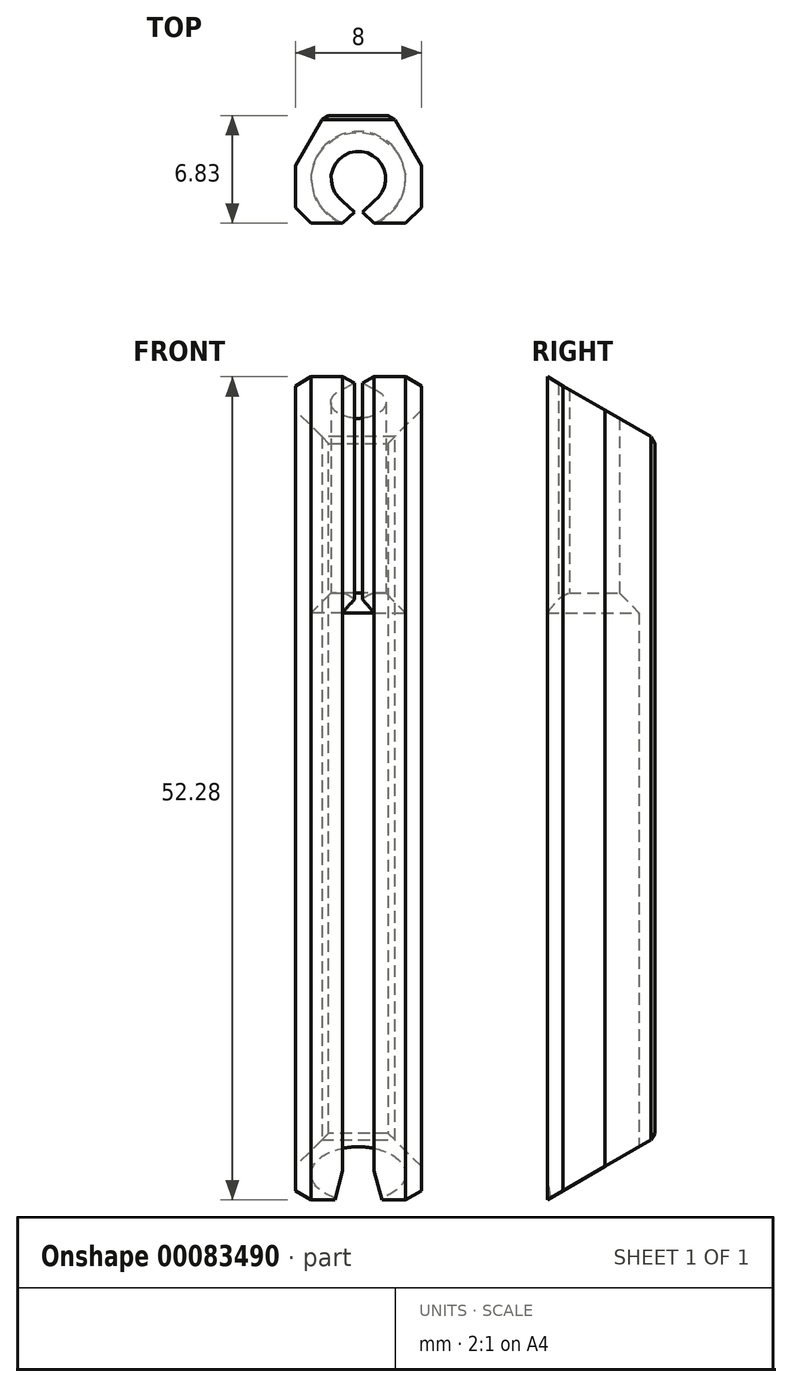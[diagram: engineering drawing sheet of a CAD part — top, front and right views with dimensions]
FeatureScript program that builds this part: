
annotation { "Feature Type Name" : "Feature", "Feature Type Description" : "" }
export const myFeature = defineFeature(function(context is Context, id is Id, definition is map)
    precondition{}
    {
        {
            var Q0;
            Q0=qCreatedBy(makeId("Top.planeOp"),FACE);
            var sketch = newSketch(context, id + "F0", { "sketchPlane" : qUnion([Q0])});
            skArc(sketch, "E0", {"start": v(1, -2.83) * mm, "mid": v(0, 3) * mm, "end": v(-1, -2.83) * mm});
            skLineSegment(sketch, "E1", {"start": v(-1, -3) * mm, "end": v(1, -3) * mm, "construction": true});
            skPoint(sketch, "E2", {"position": v(0, -3) * mm});
            skLineSegment(sketch, "E3", {"start": v(0, -3) * mm, "end": v(0, 4) * mm, "construction": true});
            skLineSegment(sketch, "E4", {"start": v(-1, -3) * mm, "end": v(-1, -2.83) * mm});
            skLineSegment(sketch, "E5", {"start": v(-1, -3) * mm, "end": v(-4, -3) * mm});
            skLineSegment(sketch, "E6", {"start": v(-4, -3) * mm, "end": v(-4, 4) * mm});
            skLineSegment(sketch, "E7", {"start": v(-4, 4) * mm, "end": v(0, 4) * mm});
            skLineSegment(sketch, "E8.MirrorCS", {"start": v(4, 4) * mm, "end": v(0, 4) * mm});
            skLineSegment(sketch, "E9.MirrorCS", {"start": v(4, -3) * mm, "end": v(4, 4) * mm});
            skLineSegment(sketch, "E10.MirrorCS", {"start": v(1, -3) * mm, "end": v(4, -3) * mm});
            skLineSegment(sketch, "E11.MirrorCS", {"start": v(1, -3) * mm, "end": v(1, -2.83) * mm});
            skPoint(sketch, "E12", {"position": v(0, 3) * mm});
            skSolve(sketch);
        }
        {
            var Q0;
            Q0 = qSketchRegion(id + "F0", true);
            extrude(context, id + "F1", {"entities" : qUnion([Q0]), "depth" : 20 * mm});
        }
        {
            var Q0;
            Q0=makeQuery(id+"F1.opExtrude","CAP_FACE",FACE,{"disambiguationData":[OSD([sQuery(id+"F0.wireOp",EDGE,"E0"),sQuery(id+"F0.wireOp",EDGE,"E4"),sQuery(id+"F0.wireOp",EDGE,"E5"),sQuery(id+"F0.wireOp",EDGE,"E6"),sQuery(id+"F0.wireOp",EDGE,"E7"),sQuery(id+"F0.wireOp",EDGE,"E8.MirrorCS"),sQuery(id+"F0.wireOp",EDGE,"E9.MirrorCS"),sQuery(id+"F0.wireOp",EDGE,"E10.MirrorCS"),sQuery(id+"F0.wireOp",EDGE,"E11.MirrorCS")])],"isStart":false});
            extrude(context, id + "F2", {"entities" : qUnion([Q0]), "operationType" : NewBodyOperationType.ADD, "depth" : 15 * mm});
        }
        {
            var Q0;
            Q0=makeQuery(id+"F2.opExtrude","CAP_FACE",FACE,{"disambiguationData":[OSD([sQuery(id+"F0.wireOp",EDGE,"E0"),sQuery(id+"F0.wireOp",EDGE,"E4"),sQuery(id+"F0.wireOp",EDGE,"E5"),sQuery(id+"F0.wireOp",EDGE,"E6"),sQuery(id+"F0.wireOp",EDGE,"E7"),sQuery(id+"F0.wireOp",EDGE,"E8.MirrorCS"),sQuery(id+"F0.wireOp",EDGE,"E9.MirrorCS"),sQuery(id+"F0.wireOp",EDGE,"E10.MirrorCS"),sQuery(id+"F0.wireOp",EDGE,"E11.MirrorCS")])],"isStart":false});
            var sketch = newSketch(context, id + "F3", { "sketchPlane" : qUnion([Q0])});
            skLineSegment(sketch, "E13.bottom", {"start": v(-4, -2.83) * mm, "end": v(4, -2.83) * mm});
            skLineSegment(sketch, "E13.top", {"start": v(-4, -3) * mm, "end": v(4, -3) * mm});
            skLineSegment(sketch, "E13.left", {"start": v(-4, -2.83) * mm, "end": v(-4, -3) * mm});
            skLineSegment(sketch, "E13.right", {"start": v(4, -2.83) * mm, "end": v(4, -3) * mm});
            skSolve(sketch);
        }
        {
            var Q0;
            Q0 = qSketchRegion(id + "F3", true);
            extrude(context, id + "F4", {"entities" : qUnion([Q0]), "operationType" : NewBodyOperationType.REMOVE, "endBound" : BoundingType.THROUGH_ALL, "oppositeDirection" : true, "depth" : 25 * mm});
        }
        {
            var Q0;
            Q0=makeQuery(id+"F2.opExtrude","CAP_FACE",FACE,{"disambiguationData":[OSD([sQuery(id+"F0.wireOp",EDGE,"E0"),sQuery(id+"F0.wireOp",EDGE,"E4"),sQuery(id+"F0.wireOp",EDGE,"E5"),sQuery(id+"F0.wireOp",EDGE,"E6"),sQuery(id+"F0.wireOp",EDGE,"E7"),sQuery(id+"F0.wireOp",EDGE,"E8.MirrorCS"),sQuery(id+"F0.wireOp",EDGE,"E9.MirrorCS"),sQuery(id+"F0.wireOp",EDGE,"E10.MirrorCS"),sQuery(id+"F0.wireOp",EDGE,"E11.MirrorCS")])],"isStart":false});
            var sketch = newSketch(context, id + "F5", { "sketchPlane" : qUnion([Q0])});
            skArc(sketch, "E14", {"start": v(1, -1.44) * mm, "mid": v(0, 1.75) * mm, "end": v(-1, -1.44) * mm});
            skLineSegment(sketch, "E15", {"start": v(-1, -1.44) * mm, "end": v(-0.25, -2.13) * mm});
            skLineSegment(sketch, "E16", {"start": v(-0.25, -2.13) * mm, "end": v(-1, -2.83) * mm});
            skLineSegment(sketch, "E17", {"start": v(0, -1.75) * mm, "end": v(0, -2.83) * mm, "construction": true});
            skLineSegment(sketch, "E18.MirrorCS", {"start": v(1, -1.44) * mm, "end": v(0.25, -2.13) * mm});
            skLineSegment(sketch, "E19.MirrorCS", {"start": v(0.25, -2.13) * mm, "end": v(1, -2.83) * mm});
            skLineSegment(sketch, "E20.0", {"start": v(1, -2.83) * mm, "end": v(4, -2.83) * mm});
            skLineSegment(sketch, "E20.1", {"start": v(4, -2.83) * mm, "end": v(4, 4) * mm});
            skLineSegment(sketch, "E20.2", {"start": v(4, 4) * mm, "end": v(-4, 4) * mm});
            skLineSegment(sketch, "E20.3", {"start": v(-4, -2.83) * mm, "end": v(-4, 4) * mm});
            skLineSegment(sketch, "E20.4", {"start": v(-4, -2.83) * mm, "end": v(-1, -2.83) * mm});
            skSolve(sketch);
        }
        {
            var Q0;
            Q0 = qSketchRegion(id + "F5", true);
            extrude(context, id + "F6", {"entities" : qUnion([Q0]), "operationType" : NewBodyOperationType.ADD, "depth" : 15 * mm});
        }
        {
            var Q0;
            Q0=makeQuery(id+"F6.opExtrude","CAP_EDGE",EDGE,{"disambiguationData":[OSD([sQuery(id+"F5.wireOp",EDGE,"E14")])],"isStart":true});
            chamfer(context, id + "F7", {"entities" : qUnion([Q0]), "width" : ((6 - 3.5) / 2) * mm, "tangentPropagation" : true});
        }
        {
            var Q0;
            Q0=makeQuery(id+"F1.opExtrude","CAP_FACE",FACE,{"disambiguationData":[OSD([sQuery(id+"F0.wireOp",EDGE,"E0"),sQuery(id+"F0.wireOp",EDGE,"E4"),sQuery(id+"F0.wireOp",EDGE,"E5"),sQuery(id+"F0.wireOp",EDGE,"E6"),sQuery(id+"F0.wireOp",EDGE,"E7"),sQuery(id+"F0.wireOp",EDGE,"E8.MirrorCS"),sQuery(id+"F0.wireOp",EDGE,"E9.MirrorCS"),sQuery(id+"F0.wireOp",EDGE,"E10.MirrorCS"),sQuery(id+"F0.wireOp",EDGE,"E11.MirrorCS")])],"isStart":true});
            extrude(context, id + "F8", {"entities" : qUnion([Q0]), "operationType" : NewBodyOperationType.ADD, "depth" : 7.9 * mm});
        }
        {
            var Q0;
            Q0=makeQuery(id+"F8.opExtrude","CAP_FACE",FACE,{"disambiguationData":[OSD([sQuery(id+"F0.wireOp",EDGE,"E0"),sQuery(id+"F0.wireOp",EDGE,"E4"),sQuery(id+"F0.wireOp",EDGE,"E5"),sQuery(id+"F0.wireOp",EDGE,"E6"),sQuery(id+"F0.wireOp",EDGE,"E7"),sQuery(id+"F0.wireOp",EDGE,"E8.MirrorCS"),sQuery(id+"F0.wireOp",EDGE,"E9.MirrorCS"),sQuery(id+"F0.wireOp",EDGE,"E10.MirrorCS"),sQuery(id+"F0.wireOp",EDGE,"E11.MirrorCS")])],"isStart":false});
            var sketch = newSketch(context, id + "F9", { "sketchPlane" : qUnion([Q0])});
            skLineSegment(sketch, "E21.bottom", {"start": v(-4, -4) * mm, "end": v(4, -4) * mm});
            skLineSegment(sketch, "E21.top", {"start": v(-4, 2.83) * mm, "end": v(4, 2.83) * mm});
            skLineSegment(sketch, "E21.left", {"start": v(-4, -4) * mm, "end": v(-4, 2.83) * mm});
            skLineSegment(sketch, "E21.right", {"start": v(4, -4) * mm, "end": v(4, 2.83) * mm});
            skSolve(sketch);
        }
        {
            var Q0;
            Q0 = qSketchRegion(id + "F9", true);
            extrude(context, id + "F10", {"entities" : qUnion([Q0]), "operationType" : NewBodyOperationType.ADD, "depth" : 3 * mm});
        }
        {
            var Q0;
            {var subQ0=sQuery(id+"F0.wireOp",EDGE,"E6");Q0=makeQuery(id+"F10.boolean.opBoolean","MERGE",FACE,{"derivedFrom":[makeQuery(id+"F8.boolean.opBoolean","MERGE",FACE,{"derivedFrom":[makeQuery(id+"F6.boolean.opBoolean","MERGE",FACE,{"derivedFrom":[makeQuery(id+"F2.boolean.opBoolean","MERGE",FACE,{"derivedFrom":[makeQuery(id+"F1.opExtrude","SWEPT_FACE",FACE,{"disambiguationData":[OSD([subQ0])]}),makeQuery(id+"F2.opExtrude","SWEPT_FACE",FACE,{"disambiguationData":[OSD([subQ0])]})]}),makeQuery(id+"F6.opExtrude","SWEPT_FACE",FACE,{"disambiguationData":[OSD([sQuery(id+"F5.wireOp",EDGE,"E20.3")])]})]}),makeQuery(id+"F8.opExtrude","SWEPT_FACE",FACE,{"disambiguationData":[OSD([subQ0])]})]}),makeQuery(id+"F10.opExtrude","SWEPT_FACE",FACE,{"disambiguationData":[OSD([sQuery(id+"F9.wireOp",EDGE,"E21.left")])]})]});}
            var sketch = newSketch(context, id + "F11", { "sketchPlane" : qUnion([Q0])});
            skLineSegment(sketch, "E22", {"start": v(-5, -12.23) * mm, "end": v(-5, 5.13) * mm});
            skLineSegment(sketch, "E23", {"start": v(-5, 5.13) * mm, "end": v(-2.5, 0.8) * mm});
            skLineSegment(sketch, "E24", {"start": v(-2.5, 0.8) * mm, "end": v(-2.5, -7.9) * mm});
            skLineSegment(sketch, "E25", {"start": v(-2.5, -7.9) * mm, "end": v(-5, -12.23) * mm});
            skLineSegment(sketch, "E26.0", {"start": v(-3, -7.9) * mm, "end": v(2.83, -7.9) * mm, "construction": true});
            skLineSegment(sketch, "E27.0", {"start": v(0, -15.9) * mm, "end": v(-5, -15.9) * mm, "construction": true});
            skSolve(sketch);
        }
        {
            var Q0;
            {var subQ0=sQuery(id+"F3.wireOp",EDGE,"E13.bottom");var subQ1=makeQuery(id+"F4.opExtrude","SWEPT_FACE",FACE,{"disambiguationData":[OSD([subQ0])]});var subQ2=sQuery(id+"F0.wireOp",EDGE,"E11.MirrorCS");var subQ3=sQuery(id+"F0.wireOp",EDGE,"E10.MirrorCS");var subQ4=sQuery(id+"F0.wireOp",EDGE,"E9.MirrorCS");var subQ5=sQuery(id+"F0.wireOp",EDGE,"E8.MirrorCS");var subQ6=sQuery(id+"F0.wireOp",EDGE,"E7");var subQ7=sQuery(id+"F0.wireOp",EDGE,"E6");var subQ8=sQuery(id+"F0.wireOp",EDGE,"E5");var subQ9=sQuery(id+"F0.wireOp",EDGE,"E4");var subQ10=sQuery(id+"F0.wireOp",EDGE,"E0");var subQ11=makeQuery(id+"F1.opExtrude","CAP_FACE",FACE,{"disambiguationData":[OSD([subQ10,subQ9,subQ8,subQ7,subQ6,subQ5,subQ4,subQ3,subQ2])],"isStart":true});Q0=makeQuery(id+"F10.boolean.opBoolean","MERGE",FACE,{"derivedFrom":[makeQuery(id+"F8.boolean.opBoolean","MERGE",FACE,{"derivedFrom":[makeQuery(id+"F6.boolean.opBoolean","MERGE",FACE,{"derivedFrom":[makeQuery(id+"F4.boolean.opBoolean","COPY",FACE,{"disambiguationData":[TD([makeQuery(id+"F1.opExtrude","SWEPT_FACE",FACE,{"disambiguationData":[OSD([subQ7])]})])],"derivedFrom":subQ1}),makeQuery(id+"F6.opExtrude","SWEPT_FACE",FACE,{"disambiguationData":[OSD([sQuery(id+"F5.wireOp",EDGE,"E20.4")])]})]}),makeQuery(id+"F8.opExtrude","SWEPT_FACE",FACE,{"disambiguationData":[OSD([subQ10,subQ9,subQ8,subQ7,subQ6,subQ5,subQ4,subQ3,subQ2,subQ0]),TDD([makeQuery(id+"F4.boolean.opBoolean","INTERSECT",EDGE,{"disambiguationData":[OD(1.0)],"derivedFrom":[subQ11,subQ1]})])]})]}),makeQuery(id+"F8.boolean.opBoolean","MERGE",FACE,{"derivedFrom":[makeQuery(id+"F6.boolean.opBoolean","MERGE",FACE,{"derivedFrom":[makeQuery(id+"F4.boolean.opBoolean","COPY",FACE,{"disambiguationData":[TD([makeQuery(id+"F1.opExtrude","SWEPT_FACE",FACE,{"disambiguationData":[OSD([subQ4])]})])],"derivedFrom":subQ1}),makeQuery(id+"F6.opExtrude","SWEPT_FACE",FACE,{"disambiguationData":[OSD([sQuery(id+"F5.wireOp",EDGE,"E20.0")])]})]}),makeQuery(id+"F8.opExtrude","SWEPT_FACE",FACE,{"disambiguationData":[OSD([subQ10,subQ9,subQ8,subQ7,subQ6,subQ5,subQ4,subQ3,subQ2,subQ0]),TDD([makeQuery(id+"F4.boolean.opBoolean","INTERSECT",EDGE,{"disambiguationData":[OD(0.0)],"derivedFrom":[subQ11,subQ1]})])]})]}),makeQuery(id+"F10.opExtrude","SWEPT_FACE",FACE,{"disambiguationData":[OSD([sQuery(id+"F9.wireOp",EDGE,"E21.top")])]})]});}
            var sketch = newSketch(context, id + "F12", { "sketchPlane" : qUnion([Q0])});
            skLineSegment(sketch, "E28.0", {"start": v(-3, -7.9) * mm, "end": v(-3, -7.9) * mm});
            skLineSegment(sketch, "E29.0", {"start": v(-3, -7.9) * mm, "end": v(1, -7.9) * mm});
            skLineSegment(sketch, "E30.0", {"start": v(1, -7.9) * mm, "end": v(3, -7.9) * mm});
            skLineSegment(sketch, "E31", {"start": v(-3, -7.9) * mm, "end": v(0, 3.3) * mm});
            skLineSegment(sketch, "E32", {"start": v(0, 3.3) * mm, "end": v(3, -7.9) * mm});
            skSolve(sketch);
        }
        {
            var Q0;
            Q0 = qSketchRegion(id + "F12", true);
            extrude(context, id + "F13", {"entities" : qUnion([Q0]), "operationType" : NewBodyOperationType.REMOVE, "oppositeDirection" : true, "depth" : 3 * mm});
        }
        {
            var Q0;
            {var subQ5=sQuery(id+"F11.wireOp",EDGE,"E23");Q0=makeQuery(id+"F11.imprint","IMPRINT",FACE,{"disambiguationData":[TD([[makeQuery(id+"F11.imprint","IMPRINT",EDGE,{"derivedFrom":subQ5}),1.0]])]});}
            var sketch = newSketch(context, id + "F14", { "sketchPlane" : qUnion([Q0])});
            skLineSegment(sketch, "E33", {"start": v(2.83, 50) * mm, "end": v(-4, 46.06) * mm});
            skLineSegment(sketch, "E34", {"start": v(-4, 46.06) * mm, "end": v(-4, 50) * mm});
            skLineSegment(sketch, "E35", {"start": v(-4, 50) * mm, "end": v(2.83, 50) * mm});
            skSolve(sketch);
        }
        {
            var Q0;
            Q0 = qSketchRegion(id + "F14", true);
            extrude(context, id + "F15", {"entities" : qUnion([Q0]), "operationType" : NewBodyOperationType.REMOVE, "endBound" : BoundingType.THROUGH_ALL, "oppositeDirection" : true, "depth" : 25 * mm});
        }
        {
            var Q0;
            Q0=makeQuery(id+"F10.opExtrude","CAP_FACE",FACE,{"disambiguationData":[OSD([sQuery(id+"F9.wireOp",EDGE,"E21.bottom"),sQuery(id+"F9.wireOp",EDGE,"E21.top"),sQuery(id+"F9.wireOp",EDGE,"E21.left"),sQuery(id+"F9.wireOp",EDGE,"E21.right")])],"isStart":false});
            var sketch = newSketch(context, id + "F16", { "sketchPlane" : qUnion([Q0])});
            skLineSegment(sketch, "E36", {"start": v(-4, 2.83) * mm, "end": v(-4, -0.83) * mm, "construction": true});
            skLineSegment(sketch, "E37", {"start": v(-4, -0.83) * mm, "end": v(-2.17, -4) * mm});
            skLineSegment(sketch, "E38", {"start": v(-2.17, -4) * mm, "end": v(2.17, -4) * mm});
            skLineSegment(sketch, "E39", {"start": v(2.17, -4) * mm, "end": v(4, -0.83) * mm});
            skLineSegment(sketch, "E40", {"start": v(4, -0.83) * mm, "end": v(4, 2.83) * mm, "construction": true});
            skLineSegment(sketch, "E41", {"start": v(4, -0.83) * mm, "end": v(4, -4) * mm});
            skLineSegment(sketch, "E42", {"start": v(4, -4) * mm, "end": v(2.17, -4) * mm});
            skLineSegment(sketch, "E43", {"start": v(-2.17, -4) * mm, "end": v(-4, -4) * mm});
            skLineSegment(sketch, "E44", {"start": v(-4, -4) * mm, "end": v(-4, -0.83) * mm});
            skSolve(sketch);
        }
        {
            var Q0;
            Q0 = qSketchRegion(id + "F16", true);
            extrude(context, id + "F17", {"entities" : qUnion([Q0]), "operationType" : NewBodyOperationType.REMOVE, "endBound" : BoundingType.THROUGH_ALL, "oppositeDirection" : true, "depth" : 25 * mm});
        }
        {
            var Q0;
            {var subQ0=sQuery(id+"F0.wireOp",EDGE,"E9.MirrorCS");Q0=makeQuery(id+"F10.boolean.opBoolean","MERGE",FACE,{"derivedFrom":[makeQuery(id+"F8.boolean.opBoolean","MERGE",FACE,{"derivedFrom":[makeQuery(id+"F6.boolean.opBoolean","MERGE",FACE,{"derivedFrom":[makeQuery(id+"F2.boolean.opBoolean","MERGE",FACE,{"derivedFrom":[makeQuery(id+"F1.opExtrude","SWEPT_FACE",FACE,{"disambiguationData":[OSD([subQ0])]}),makeQuery(id+"F2.opExtrude","SWEPT_FACE",FACE,{"disambiguationData":[OSD([subQ0])]})]}),makeQuery(id+"F6.opExtrude","SWEPT_FACE",FACE,{"disambiguationData":[OSD([sQuery(id+"F5.wireOp",EDGE,"E20.1")])]})]}),makeQuery(id+"F8.opExtrude","SWEPT_FACE",FACE,{"disambiguationData":[OSD([subQ0])]})]}),makeQuery(id+"F10.opExtrude","SWEPT_FACE",FACE,{"disambiguationData":[OSD([sQuery(id+"F9.wireOp",EDGE,"E21.right")])]})]});}
            var sketch = newSketch(context, id + "F18", { "sketchPlane" : qUnion([Q0])});
            skLineSegment(sketch, "E45.0", {"start": v(-2.83, -7.9) * mm, "end": v(-2.83, 50) * mm, "construction": true});
            skLineSegment(sketch, "E46", {"start": v(-2.83, -2.28) * mm, "end": v(4, 1.67) * mm});
            skLineSegment(sketch, "E47", {"start": v(-2.83, -2.28) * mm, "end": v(-2.83, -10.9) * mm});
            skLineSegment(sketch, "E48", {"start": v(-2.83, -10.9) * mm, "end": v(4, -10.9) * mm});
            skLineSegment(sketch, "E49", {"start": v(4, -10.9) * mm, "end": v(4, 1.67) * mm});
            skSolve(sketch);
        }
        {
            var Q0;
            Q0 = qSketchRegion(id + "F18", true);
            extrude(context, id + "F19", {"entities" : qUnion([Q0]), "operationType" : NewBodyOperationType.REMOVE, "endBound" : BoundingType.THROUGH_ALL, "oppositeDirection" : true, "depth" : 25 * mm});
        }
        {
            var Q0;
            {var subQ0=sQuery(id+"F3.wireOp",EDGE,"E13.bottom");var subQ1=sQuery(id+"F0.wireOp",EDGE,"E11.MirrorCS");var subQ2=sQuery(id+"F0.wireOp",EDGE,"E10.MirrorCS");var subQ3=sQuery(id+"F0.wireOp",EDGE,"E9.MirrorCS");var subQ4=sQuery(id+"F0.wireOp",EDGE,"E8.MirrorCS");var subQ5=sQuery(id+"F0.wireOp",EDGE,"E7");var subQ6=sQuery(id+"F0.wireOp",EDGE,"E6");var subQ7=sQuery(id+"F0.wireOp",EDGE,"E5");var subQ8=sQuery(id+"F0.wireOp",EDGE,"E4");var subQ9=sQuery(id+"F0.wireOp",EDGE,"E0");Q0=makeQuery(id+"F10.boolean.opBoolean","MERGE",EDGE,{"derivedFrom":[makeQuery(id+"F8.boolean.opBoolean","MERGE",EDGE,{"derivedFrom":[makeQuery(id+"F6.boolean.opBoolean","MERGE",EDGE,{"derivedFrom":[makeQuery(id+"F4.boolean.opBoolean","COPY",EDGE,{"derivedFrom":makeQuery(id+"F4.opExtrude","SWEPT_EDGE",EDGE,{"disambiguationData":[OSD([subQ6,subQ0,sQuery(id+"F3.wireOp",EDGE,"E13.left")])]})}),makeQuery(id+"F6.opExtrude","SWEPT_EDGE",EDGE,{"disambiguationData":[OSD([sQuery(id+"F5.wireOp",EDGE,"E20.3"),sQuery(id+"F5.wireOp",EDGE,"E20.4")])]})]}),makeQuery(id+"F8.opExtrude","SWEPT_EDGE",EDGE,{"disambiguationData":[OSD([subQ9,subQ8,subQ7,subQ6,subQ5,subQ4,subQ3,subQ2,subQ1,subQ0]),TDD([makeQuery(id+"F4.boolean.opBoolean","INTERSECT",VERTEX,{"disambiguationData":[OD(0.0)],"derivedFrom":[makeQuery(id+"F1.opExtrude","CAP_FACE",FACE,{"disambiguationData":[OSD([subQ9,subQ8,subQ7,subQ6,subQ5,subQ4,subQ3,subQ2,subQ1])],"isStart":true}),makeQuery(id+"F4.opExtrude","SWEPT_FACE",FACE,{"disambiguationData":[OSD([subQ0])]})]})])]})]}),makeQuery(id+"F10.opExtrude","SWEPT_EDGE",EDGE,{"disambiguationData":[OSD([sQuery(id+"F9.wireOp",EDGE,"E21.top"),sQuery(id+"F9.wireOp",EDGE,"E21.left")])]})]});}
            var Q1;
            {var subQ0=sQuery(id+"F3.wireOp",EDGE,"E13.bottom");var subQ1=sQuery(id+"F0.wireOp",EDGE,"E11.MirrorCS");var subQ2=sQuery(id+"F0.wireOp",EDGE,"E10.MirrorCS");var subQ3=sQuery(id+"F0.wireOp",EDGE,"E9.MirrorCS");var subQ4=sQuery(id+"F0.wireOp",EDGE,"E8.MirrorCS");var subQ5=sQuery(id+"F0.wireOp",EDGE,"E7");var subQ6=sQuery(id+"F0.wireOp",EDGE,"E6");var subQ7=sQuery(id+"F0.wireOp",EDGE,"E5");var subQ8=sQuery(id+"F0.wireOp",EDGE,"E4");var subQ9=sQuery(id+"F0.wireOp",EDGE,"E0");Q1=makeQuery(id+"F10.boolean.opBoolean","MERGE",EDGE,{"derivedFrom":[makeQuery(id+"F8.boolean.opBoolean","MERGE",EDGE,{"derivedFrom":[makeQuery(id+"F6.boolean.opBoolean","MERGE",EDGE,{"derivedFrom":[makeQuery(id+"F4.boolean.opBoolean","COPY",EDGE,{"derivedFrom":makeQuery(id+"F4.opExtrude","SWEPT_EDGE",EDGE,{"disambiguationData":[OSD([subQ3,subQ0,sQuery(id+"F3.wireOp",EDGE,"E13.right")])]})}),makeQuery(id+"F6.opExtrude","SWEPT_EDGE",EDGE,{"disambiguationData":[OSD([sQuery(id+"F5.wireOp",EDGE,"E20.0"),sQuery(id+"F5.wireOp",EDGE,"E20.1")])]})]}),makeQuery(id+"F8.opExtrude","SWEPT_EDGE",EDGE,{"disambiguationData":[OSD([subQ9,subQ8,subQ7,subQ6,subQ5,subQ4,subQ3,subQ2,subQ1,subQ0]),TDD([makeQuery(id+"F4.boolean.opBoolean","INTERSECT",VERTEX,{"disambiguationData":[OD(1.0)],"derivedFrom":[makeQuery(id+"F1.opExtrude","CAP_FACE",FACE,{"disambiguationData":[OSD([subQ9,subQ8,subQ7,subQ6,subQ5,subQ4,subQ3,subQ2,subQ1])],"isStart":true}),makeQuery(id+"F4.opExtrude","SWEPT_FACE",FACE,{"disambiguationData":[OSD([subQ0])]})]})])]})]}),makeQuery(id+"F10.opExtrude","SWEPT_EDGE",EDGE,{"disambiguationData":[OSD([sQuery(id+"F9.wireOp",EDGE,"E21.top"),sQuery(id+"F9.wireOp",EDGE,"E21.right")])]})]});}
            chamfer(context, id + "F20", {"entities" : qUnion([Q0, Q1]), "width" : 1 * mm, "tangentPropagation" : true});
        }
        {
            var Q0;
            {var subQ0=sQuery(id+"F0.wireOp",EDGE,"E8.MirrorCS");var subQ1=sQuery(id+"F0.wireOp",EDGE,"E7");Q0=makeQuery(id+"F10.boolean.opBoolean","MERGE",FACE,{"derivedFrom":[makeQuery(id+"F8.boolean.opBoolean","MERGE",FACE,{"derivedFrom":[makeQuery(id+"F6.boolean.opBoolean","MERGE",FACE,{"derivedFrom":[makeQuery(id+"F2.boolean.opBoolean","MERGE",FACE,{"derivedFrom":[makeQuery(id+"F1.opExtrude","SWEPT_FACE",FACE,{"disambiguationData":[OSD([subQ1,subQ0])]}),makeQuery(id+"F2.opExtrude","SWEPT_FACE",FACE,{"disambiguationData":[OSD([subQ1,subQ0])]})]}),makeQuery(id+"F6.opExtrude","SWEPT_FACE",FACE,{"disambiguationData":[OSD([sQuery(id+"F5.wireOp",EDGE,"E20.2")])]})]}),makeQuery(id+"F8.opExtrude","SWEPT_FACE",FACE,{"disambiguationData":[OSD([subQ1,subQ0])]})]}),makeQuery(id+"F10.opExtrude","SWEPT_FACE",FACE,{"disambiguationData":[OSD([sQuery(id+"F9.wireOp",EDGE,"E21.bottom")])]})]});}
            chamfer(context, id + "F21", {"entities" : qUnion([Q0]), "width" : 0.5 * mm, "tangentPropagation" : true});
        }
    });
